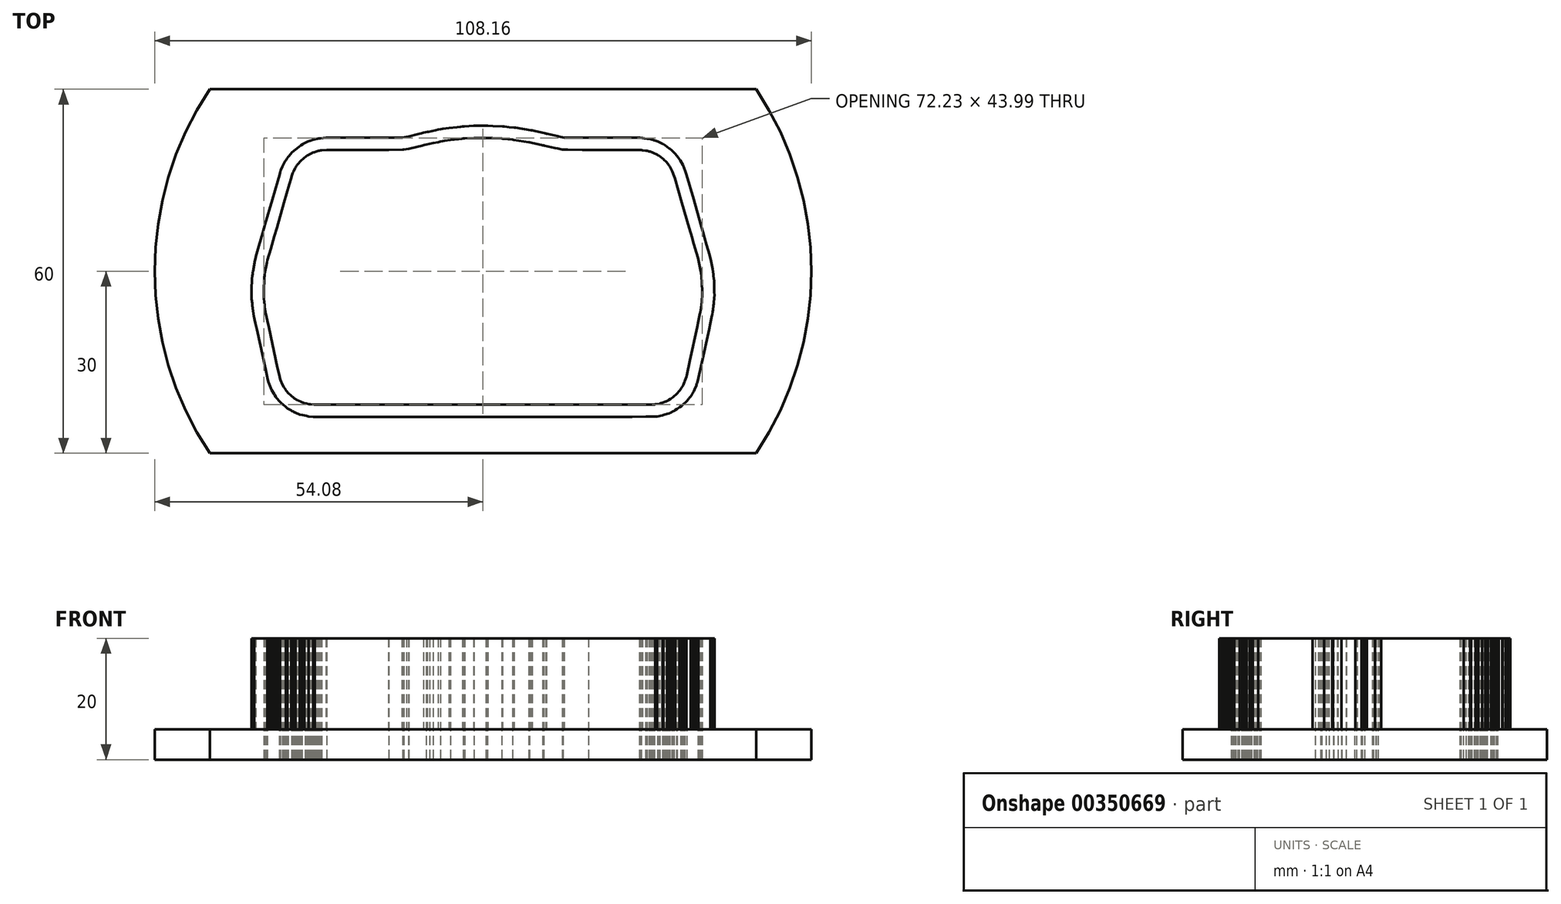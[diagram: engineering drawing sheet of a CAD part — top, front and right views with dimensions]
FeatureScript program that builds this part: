
annotation { "Feature Type Name" : "Feature", "Feature Type Description" : "" }
export const myFeature = defineFeature(function(context is Context, id is Id, definition is map)
    precondition{}
    {
        {
            var Q0;
            Q0=qCreatedBy(makeId("Top.planeOp"),FACE);
            var sketch = newSketch(context, id + "F0", { "sketchPlane" : qUnion([Q0])});
            skLineSegment(sketch, "E0.bottom", {"start": v(-45, 30) * mm, "end": v(45, 30) * mm});
            skLineSegment(sketch, "E0.top", {"start": v(-45, -30) * mm, "end": v(45, -30) * mm});
            skArc(sketch, "E1", {"start": v(-45, 30) * mm, "mid": v(-54.08, 0) * mm, "end": v(-45, -30) * mm});
            skArc(sketch, "E2.MirrorCS", {"start": v(45, 30) * mm, "mid": v(54.08, 0) * mm, "end": v(45, -30) * mm});
            skSolve(sketch);
        }
        {
            var Q0;
            Q0 = qSketchRegion(id + "F0", true);
            extrude(context, id + "F1", {"entities" : qUnion([Q0]), "depth" : 5 * mm});
        }
        {
            var Q0;
            Q0=makeQuery(id+"F1.opExtrude","CAP_FACE",FACE,{"disambiguationData":[OSD([sQuery(id+"F0.wireOp",EDGE,"E0.bottom"),sQuery(id+"F0.wireOp",EDGE,"E0.top"),sQuery(id+"F0.wireOp",EDGE,"E1"),sQuery(id+"F0.wireOp",EDGE,"E2.MirrorCS")])],"isStart":false});
            var sketch = newSketch(context, id + "F2", { "sketchPlane" : qUnion([Q0])});
            skLineSegment(sketch, "E3", {"start": v(-13.19, 20.04) * mm, "end": v(-13.22, 20.04) * mm});
            skLineSegment(sketch, "E4", {"start": v(-13.22, 20.04) * mm, "end": v(-15.53, 20) * mm});
            skLineSegment(sketch, "E5", {"start": v(-15.53, 20) * mm, "end": v(-16.38, 20) * mm});
            skLineSegment(sketch, "E6", {"start": v(-16.38, 20) * mm, "end": v(-22.09, 20.01) * mm});
            skLineSegment(sketch, "E7", {"start": v(-22.09, 20.01) * mm, "end": v(-24.58, 20) * mm});
            skLineSegment(sketch, "E8", {"start": v(-24.58, 20) * mm, "end": v(-25.75, 20) * mm});
            skLineSegment(sketch, "E9", {"start": v(-25.75, 20) * mm, "end": v(-26.54, 19.93) * mm});
            skLineSegment(sketch, "E10", {"start": v(-26.54, 19.93) * mm, "end": v(-26.56, 19.92) * mm});
            skLineSegment(sketch, "E11", {"start": v(-26.56, 19.92) * mm, "end": v(-26.73, 19.91) * mm});
            skLineSegment(sketch, "E12", {"start": v(-26.73, 19.91) * mm, "end": v(-26.77, 19.9) * mm});
            skLineSegment(sketch, "E13", {"start": v(-26.77, 19.9) * mm, "end": v(-26.93, 19.87) * mm});
            skLineSegment(sketch, "E14", {"start": v(-26.93, 19.87) * mm, "end": v(-27.02, 19.84) * mm});
            skLineSegment(sketch, "E15", {"start": v(-27.02, 19.84) * mm, "end": v(-27.07, 19.84) * mm});
            skLineSegment(sketch, "E16", {"start": v(-27.07, 19.84) * mm, "end": v(-27.29, 19.8) * mm});
            skLineSegment(sketch, "E17", {"start": v(-27.29, 19.8) * mm, "end": v(-27.43, 19.75) * mm});
            skLineSegment(sketch, "E18", {"start": v(-27.43, 19.75) * mm, "end": v(-27.8, 19.62) * mm});
            skLineSegment(sketch, "E19", {"start": v(-27.8, 19.62) * mm, "end": v(-27.85, 19.6) * mm});
            skLineSegment(sketch, "E20", {"start": v(-27.85, 19.6) * mm, "end": v(-28.06, 19.54) * mm});
            skLineSegment(sketch, "E21", {"start": v(-28.06, 19.54) * mm, "end": v(-28.09, 19.52) * mm});
            skLineSegment(sketch, "E22", {"start": v(-28.09, 19.52) * mm, "end": v(-28.16, 19.49) * mm});
            skLineSegment(sketch, "E23", {"start": v(-28.16, 19.49) * mm, "end": v(-28.67, 19.22) * mm});
            skLineSegment(sketch, "E24", {"start": v(-28.67, 19.22) * mm, "end": v(-28.75, 19.18) * mm});
            skLineSegment(sketch, "E25", {"start": v(-28.75, 19.18) * mm, "end": v(-28.93, 19.09) * mm});
            skLineSegment(sketch, "E26", {"start": v(-28.93, 19.09) * mm, "end": v(-29.1, 18.96) * mm});
            skLineSegment(sketch, "E27", {"start": v(-29.1, 18.96) * mm, "end": v(-30, 18.23) * mm});
            skLineSegment(sketch, "E28", {"start": v(-30, 18.23) * mm, "end": v(-30.47, 17.64) * mm});
            skLineSegment(sketch, "E29", {"start": v(-30.47, 17.64) * mm, "end": v(-30.6, 17.5) * mm});
            skLineSegment(sketch, "E30", {"start": v(-30.6, 17.5) * mm, "end": v(-30.67, 17.42) * mm});
            skLineSegment(sketch, "E31", {"start": v(-30.67, 17.42) * mm, "end": v(-30.74, 17.3) * mm});
            skLineSegment(sketch, "E32", {"start": v(-30.74, 17.3) * mm, "end": v(-30.9, 17.07) * mm});
            skLineSegment(sketch, "E33", {"start": v(-30.9, 17.07) * mm, "end": v(-30.92, 17.02) * mm});
            skLineSegment(sketch, "E34", {"start": v(-30.92, 17.02) * mm, "end": v(-30.93, 17.01) * mm});
            skLineSegment(sketch, "E35", {"start": v(-30.93, 17.01) * mm, "end": v(-31.22, 16.41) * mm});
            skLineSegment(sketch, "E36", {"start": v(-31.22, 16.41) * mm, "end": v(-31.31, 16.22) * mm});
            skLineSegment(sketch, "E37", {"start": v(-31.31, 16.22) * mm, "end": v(-31.31, 16.22) * mm});
            skLineSegment(sketch, "E38", {"start": v(-31.31, 16.22) * mm, "end": v(-31.44, 15.86) * mm});
            skLineSegment(sketch, "E39", {"start": v(-31.44, 15.86) * mm, "end": v(-31.5, 15.65) * mm});
            skLineSegment(sketch, "E40", {"start": v(-31.5, 15.65) * mm, "end": v(-31.58, 15.39) * mm});
            skLineSegment(sketch, "E41", {"start": v(-31.58, 15.39) * mm, "end": v(-31.89, 14.33) * mm});
            skLineSegment(sketch, "E42", {"start": v(-31.89, 14.33) * mm, "end": v(-32.77, 11.28) * mm});
            skLineSegment(sketch, "E43", {"start": v(-32.77, 11.28) * mm, "end": v(-33.95, 7.2) * mm});
            skLineSegment(sketch, "E44", {"start": v(-33.95, 7.2) * mm, "end": v(-34.35, 5.79) * mm});
            skLineSegment(sketch, "E45", {"start": v(-34.35, 5.79) * mm, "end": v(-34.96, 3.66) * mm});
            skLineSegment(sketch, "E46", {"start": v(-34.96, 3.66) * mm, "end": v(-35.48, 1.86) * mm});
            skLineSegment(sketch, "E47", {"start": v(-35.48, 1.86) * mm, "end": v(-35.5, 1.82) * mm});
            skLineSegment(sketch, "E48", {"start": v(-35.5, 1.82) * mm, "end": v(-35.58, 1.44) * mm});
            skLineSegment(sketch, "E49", {"start": v(-35.58, 1.44) * mm, "end": v(-35.94, -0.4) * mm});
            skLineSegment(sketch, "E50", {"start": v(-35.94, -0.4) * mm, "end": v(-35.94, -0.42) * mm});
            skLineSegment(sketch, "E51", {"start": v(-35.94, -0.42) * mm, "end": v(-35.97, -0.7) * mm});
            skLineSegment(sketch, "E52", {"start": v(-35.97, -0.7) * mm, "end": v(-36, -1) * mm});
            skLineSegment(sketch, "E53", {"start": v(-36, -1) * mm, "end": v(-36.05, -1.36) * mm});
            skLineSegment(sketch, "E54", {"start": v(-36.05, -1.36) * mm, "end": v(-36.1, -3.07) * mm});
            skLineSegment(sketch, "E55", {"start": v(-36.1, -3.07) * mm, "end": v(-36.11, -3.77) * mm});
            skLineSegment(sketch, "E56", {"start": v(-36.11, -3.77) * mm, "end": v(-36.09, -4.44) * mm});
            skLineSegment(sketch, "E57", {"start": v(-36.09, -4.44) * mm, "end": v(-36.02, -5.1) * mm});
            skLineSegment(sketch, "E58", {"start": v(-36.02, -5.1) * mm, "end": v(-35.98, -5.52) * mm});
            skLineSegment(sketch, "E59", {"start": v(-35.98, -5.52) * mm, "end": v(-35.95, -5.78) * mm});
            skLineSegment(sketch, "E60", {"start": v(-35.95, -5.78) * mm, "end": v(-35.94, -5.86) * mm});
            skLineSegment(sketch, "E61", {"start": v(-35.94, -5.86) * mm, "end": v(-35.75, -7.07) * mm});
            skLineSegment(sketch, "E62", {"start": v(-35.75, -7.07) * mm, "end": v(-35.7, -7.25) * mm});
            skLineSegment(sketch, "E63", {"start": v(-35.7, -7.25) * mm, "end": v(-35.64, -7.56) * mm});
            skLineSegment(sketch, "E64", {"start": v(-35.64, -7.56) * mm, "end": v(-35.52, -8.14) * mm});
            skLineSegment(sketch, "E65", {"start": v(-35.52, -8.14) * mm, "end": v(-35.29, -9.19) * mm});
            skLineSegment(sketch, "E66", {"start": v(-35.29, -9.19) * mm, "end": v(-33.84, -15.86) * mm});
            skLineSegment(sketch, "E67", {"start": v(-33.84, -15.86) * mm, "end": v(-33.57, -17.1) * mm});
            skLineSegment(sketch, "E68", {"start": v(-33.57, -17.1) * mm, "end": v(-33.5, -17.38) * mm});
            skLineSegment(sketch, "E69", {"start": v(-33.5, -17.38) * mm, "end": v(-33.42, -17.7) * mm});
            skLineSegment(sketch, "E70", {"start": v(-33.42, -17.7) * mm, "end": v(-33.34, -17.9) * mm});
            skLineSegment(sketch, "E71", {"start": v(-33.34, -17.9) * mm, "end": v(-33.05, -18.64) * mm});
            skLineSegment(sketch, "E72", {"start": v(-33.05, -18.64) * mm, "end": v(-32.77, -19.1) * mm});
            skLineSegment(sketch, "E73", {"start": v(-32.77, -19.1) * mm, "end": v(-32.76, -19.1) * mm});
            skLineSegment(sketch, "E74", {"start": v(-32.76, -19.1) * mm, "end": v(-32.57, -19.4) * mm});
            skLineSegment(sketch, "E75", {"start": v(-32.57, -19.4) * mm, "end": v(-32.5, -19.55) * mm});
            skLineSegment(sketch, "E76", {"start": v(-32.5, -19.55) * mm, "end": v(-32.44, -19.6) * mm});
            skLineSegment(sketch, "E77", {"start": v(-32.44, -19.6) * mm, "end": v(-32.24, -19.84) * mm});
            skLineSegment(sketch, "E78", {"start": v(-32.24, -19.84) * mm, "end": v(-32.12, -20.01) * mm});
            skLineSegment(sketch, "E79", {"start": v(-32.12, -20.01) * mm, "end": v(-32.06, -20.08) * mm});
            skLineSegment(sketch, "E80", {"start": v(-32.06, -20.08) * mm, "end": v(-32, -20.13) * mm});
            skLineSegment(sketch, "E81", {"start": v(-32, -20.13) * mm, "end": v(-31.69, -20.4) * mm});
            skLineSegment(sketch, "E82", {"start": v(-31.69, -20.4) * mm, "end": v(-31.58, -20.5) * mm});
            skLineSegment(sketch, "E83", {"start": v(-31.58, -20.5) * mm, "end": v(-31.2, -20.83) * mm});
            skLineSegment(sketch, "E84", {"start": v(-31.2, -20.83) * mm, "end": v(-31.12, -20.9) * mm});
            skLineSegment(sketch, "E85", {"start": v(-31.12, -20.9) * mm, "end": v(-31.12, -20.9) * mm});
            skLineSegment(sketch, "E86", {"start": v(-31.12, -20.9) * mm, "end": v(-31.05, -20.95) * mm});
            skLineSegment(sketch, "E87", {"start": v(-31.05, -20.95) * mm, "end": v(-30.61, -21.22) * mm});
            skLineSegment(sketch, "E88", {"start": v(-30.61, -21.22) * mm, "end": v(-30.57, -21.24) * mm});
            skLineSegment(sketch, "E89", {"start": v(-30.57, -21.24) * mm, "end": v(-30.38, -21.32) * mm});
            skLineSegment(sketch, "E90", {"start": v(-30.38, -21.32) * mm, "end": v(-30.33, -21.35) * mm});
            skLineSegment(sketch, "E91", {"start": v(-30.33, -21.35) * mm, "end": v(-30.13, -21.44) * mm});
            skLineSegment(sketch, "E92", {"start": v(-30.13, -21.44) * mm, "end": v(-30.07, -21.48) * mm});
            skLineSegment(sketch, "E93", {"start": v(-30.07, -21.48) * mm, "end": v(-30.05, -21.49) * mm});
            skLineSegment(sketch, "E94", {"start": v(-30.05, -21.49) * mm, "end": v(-29.8, -21.6) * mm});
            skLineSegment(sketch, "E95", {"start": v(-29.8, -21.6) * mm, "end": v(-29.78, -21.6) * mm});
            skLineSegment(sketch, "E96", {"start": v(-29.78, -21.6) * mm, "end": v(-29.27, -21.77) * mm});
            skLineSegment(sketch, "E97", {"start": v(-29.27, -21.77) * mm, "end": v(-29.07, -21.8) * mm});
            skLineSegment(sketch, "E98", {"start": v(-29.07, -21.8) * mm, "end": v(-28.67, -21.89) * mm});
            skLineSegment(sketch, "E99", {"start": v(-28.67, -21.89) * mm, "end": v(-28.43, -21.94) * mm});
            skLineSegment(sketch, "E100", {"start": v(-28.43, -21.94) * mm, "end": v(-27.8, -21.99) * mm});
            skLineSegment(sketch, "E101", {"start": v(-27.8, -21.99) * mm, "end": v(-27.64, -22) * mm});
            skLineSegment(sketch, "E102", {"start": v(-27.64, -22) * mm, "end": v(0.52, -22) * mm});
            skLineSegment(sketch, "E103", {"start": v(0.52, -22) * mm, "end": v(2.71, -22) * mm});
            skLineSegment(sketch, "E104", {"start": v(2.71, -22) * mm, "end": v(8.2, -22) * mm});
            skLineSegment(sketch, "E105", {"start": v(8.2, -22) * mm, "end": v(16.38, -22) * mm});
            skLineSegment(sketch, "E106", {"start": v(16.38, -22) * mm, "end": v(23.57, -22) * mm});
            skLineSegment(sketch, "E107", {"start": v(23.57, -22) * mm, "end": v(24.58, -21.99) * mm});
            skLineSegment(sketch, "E108", {"start": v(24.58, -21.99) * mm, "end": v(26.86, -21.97) * mm});
            skLineSegment(sketch, "E109", {"start": v(26.86, -21.97) * mm, "end": v(28.22, -21.96) * mm});
            skLineSegment(sketch, "E110", {"start": v(28.22, -21.96) * mm, "end": v(28.25, -21.96) * mm});
            skLineSegment(sketch, "E111", {"start": v(28.25, -21.96) * mm, "end": v(28.37, -21.94) * mm});
            skLineSegment(sketch, "E112", {"start": v(28.37, -21.94) * mm, "end": v(29.06, -21.82) * mm});
            skLineSegment(sketch, "E113", {"start": v(29.06, -21.82) * mm, "end": v(29.09, -21.81) * mm});
            skLineSegment(sketch, "E114", {"start": v(29.09, -21.81) * mm, "end": v(29.11, -21.8) * mm});
            skLineSegment(sketch, "E115", {"start": v(29.11, -21.8) * mm, "end": v(29.78, -21.6) * mm});
            skLineSegment(sketch, "E116", {"start": v(29.78, -21.6) * mm, "end": v(29.9, -21.56) * mm});
            skLineSegment(sketch, "E117", {"start": v(29.9, -21.56) * mm, "end": v(29.91, -21.55) * mm});
            skLineSegment(sketch, "E118", {"start": v(29.91, -21.55) * mm, "end": v(30.08, -21.48) * mm});
            skLineSegment(sketch, "E119", {"start": v(30.08, -21.48) * mm, "end": v(30.14, -21.45) * mm});
            skLineSegment(sketch, "E120", {"start": v(30.14, -21.45) * mm, "end": v(30.37, -21.34) * mm});
            skLineSegment(sketch, "E121", {"start": v(30.37, -21.34) * mm, "end": v(30.54, -21.26) * mm});
            skLineSegment(sketch, "E122", {"start": v(30.54, -21.26) * mm, "end": v(30.56, -21.24) * mm});
            skLineSegment(sketch, "E123", {"start": v(30.56, -21.24) * mm, "end": v(30.88, -21.03) * mm});
            skLineSegment(sketch, "E124", {"start": v(30.88, -21.03) * mm, "end": v(31.26, -20.77) * mm});
            skLineSegment(sketch, "E125", {"start": v(31.26, -20.77) * mm, "end": v(31.43, -20.66) * mm});
            skLineSegment(sketch, "E126", {"start": v(31.43, -20.66) * mm, "end": v(31.84, -20.29) * mm});
            skLineSegment(sketch, "E127", {"start": v(31.84, -20.29) * mm, "end": v(31.92, -20.22) * mm});
            skLineSegment(sketch, "E128", {"start": v(31.92, -20.22) * mm, "end": v(31.95, -20.19) * mm});
            skLineSegment(sketch, "E129", {"start": v(31.95, -20.19) * mm, "end": v(31.98, -20.16) * mm});
            skLineSegment(sketch, "E130", {"start": v(31.98, -20.16) * mm, "end": v(32.33, -19.73) * mm});
            skLineSegment(sketch, "E131", {"start": v(32.33, -19.73) * mm, "end": v(32.43, -19.61) * mm});
            skLineSegment(sketch, "E132", {"start": v(32.43, -19.61) * mm, "end": v(32.58, -19.43) * mm});
            skLineSegment(sketch, "E133", {"start": v(32.58, -19.43) * mm, "end": v(32.68, -19.27) * mm});
            skLineSegment(sketch, "E134", {"start": v(32.68, -19.27) * mm, "end": v(32.7, -19.24) * mm});
            skLineSegment(sketch, "E135", {"start": v(32.7, -19.24) * mm, "end": v(32.77, -19.13) * mm});
            skLineSegment(sketch, "E136", {"start": v(32.77, -19.13) * mm, "end": v(32.93, -18.86) * mm});
            skLineSegment(sketch, "E137", {"start": v(32.93, -18.86) * mm, "end": v(32.97, -18.77) * mm});
            skLineSegment(sketch, "E138", {"start": v(32.97, -18.77) * mm, "end": v(32.98, -18.75) * mm});
            skLineSegment(sketch, "E139", {"start": v(32.98, -18.75) * mm, "end": v(33.06, -18.58) * mm});
            skLineSegment(sketch, "E140", {"start": v(33.06, -18.58) * mm, "end": v(33.22, -18.24) * mm});
            skLineSegment(sketch, "E141", {"start": v(33.22, -18.24) * mm, "end": v(33.24, -18.2) * mm});
            skLineSegment(sketch, "E142", {"start": v(33.24, -18.2) * mm, "end": v(33.28, -18.06) * mm});
            skLineSegment(sketch, "E143", {"start": v(33.28, -18.06) * mm, "end": v(33.5, -17.4) * mm});
            skLineSegment(sketch, "E144", {"start": v(33.5, -17.4) * mm, "end": v(33.5, -17.38) * mm});
            skLineSegment(sketch, "E145", {"start": v(33.5, -17.38) * mm, "end": v(33.5, -17.38) * mm});
            skLineSegment(sketch, "E146", {"start": v(33.5, -17.38) * mm, "end": v(33.56, -17.13) * mm});
            skLineSegment(sketch, "E147", {"start": v(33.56, -17.13) * mm, "end": v(34.09, -14.66) * mm});
            skLineSegment(sketch, "E148", {"start": v(34.09, -14.66) * mm, "end": v(35.28, -9.19) * mm});
            skLineSegment(sketch, "E149", {"start": v(35.28, -9.19) * mm, "end": v(35.5, -8.17) * mm});
            skLineSegment(sketch, "E150", {"start": v(35.5, -8.17) * mm, "end": v(35.76, -6.92) * mm});
            skLineSegment(sketch, "E151", {"start": v(35.76, -6.92) * mm, "end": v(35.78, -6.78) * mm});
            skLineSegment(sketch, "E152", {"start": v(35.78, -6.78) * mm, "end": v(35.87, -6.38) * mm});
            skLineSegment(sketch, "E153", {"start": v(35.87, -6.38) * mm, "end": v(35.9, -6.07) * mm});
            skLineSegment(sketch, "E154", {"start": v(35.9, -6.07) * mm, "end": v(36, -5.42) * mm});
            skLineSegment(sketch, "E155", {"start": v(36, -5.42) * mm, "end": v(36.03, -5.15) * mm});
            skLineSegment(sketch, "E156", {"start": v(36.03, -5.15) * mm, "end": v(36.03, -5.1) * mm});
            skLineSegment(sketch, "E157", {"start": v(36.03, -5.1) * mm, "end": v(36.04, -4.94) * mm});
            skLineSegment(sketch, "E158", {"start": v(36.04, -4.94) * mm, "end": v(36.11, -3.83) * mm});
            skLineSegment(sketch, "E159", {"start": v(36.11, -3.83) * mm, "end": v(36.1, -3.51) * mm});
            skLineSegment(sketch, "E160", {"start": v(36.1, -3.51) * mm, "end": v(36.07, -1.8) * mm});
            skLineSegment(sketch, "E161", {"start": v(36.07, -1.8) * mm, "end": v(36.07, -1.7) * mm});
            skLineSegment(sketch, "E162", {"start": v(36.07, -1.7) * mm, "end": v(36, -1) * mm});
            skLineSegment(sketch, "E163", {"start": v(36, -1) * mm, "end": v(35.97, -0.72) * mm});
            skLineSegment(sketch, "E164", {"start": v(35.97, -0.72) * mm, "end": v(35.96, -0.63) * mm});
            skLineSegment(sketch, "E165", {"start": v(35.96, -0.63) * mm, "end": v(35.96, -0.62) * mm});
            skLineSegment(sketch, "E166", {"start": v(35.96, -0.62) * mm, "end": v(35.93, -0.4) * mm});
            skLineSegment(sketch, "E167", {"start": v(35.93, -0.4) * mm, "end": v(35.85, -0.02) * mm});
            skLineSegment(sketch, "E168", {"start": v(35.85, -0.02) * mm, "end": v(35.63, 1.25) * mm});
            skLineSegment(sketch, "E169", {"start": v(35.63, 1.25) * mm, "end": v(35.4, 2.2) * mm});
            skLineSegment(sketch, "E170", {"start": v(35.4, 2.2) * mm, "end": v(34.92, 3.85) * mm});
            skLineSegment(sketch, "E171", {"start": v(34.92, 3.85) * mm, "end": v(34.6, 4.94) * mm});
            skLineSegment(sketch, "E172", {"start": v(34.6, 4.94) * mm, "end": v(34.44, 5.5) * mm});
            skLineSegment(sketch, "E173", {"start": v(34.44, 5.5) * mm, "end": v(33.95, 7.2) * mm});
            skLineSegment(sketch, "E174", {"start": v(33.95, 7.2) * mm, "end": v(32.77, 11.29) * mm});
            skLineSegment(sketch, "E175", {"start": v(32.77, 11.29) * mm, "end": v(31.58, 15.39) * mm});
            skLineSegment(sketch, "E176", {"start": v(31.58, 15.39) * mm, "end": v(31.5, 15.65) * mm});
            skLineSegment(sketch, "E177", {"start": v(31.5, 15.65) * mm, "end": v(31.17, 16.51) * mm});
            skLineSegment(sketch, "E178", {"start": v(31.17, 16.51) * mm, "end": v(31.12, 16.64) * mm});
            skLineSegment(sketch, "E179", {"start": v(31.12, 16.64) * mm, "end": v(31.12, 16.65) * mm});
            skLineSegment(sketch, "E180", {"start": v(31.12, 16.65) * mm, "end": v(30.78, 17.24) * mm});
            skLineSegment(sketch, "E181", {"start": v(30.78, 17.24) * mm, "end": v(30.71, 17.35) * mm});
            skLineSegment(sketch, "E182", {"start": v(30.71, 17.35) * mm, "end": v(30.64, 17.43) * mm});
            skLineSegment(sketch, "E183", {"start": v(30.64, 17.43) * mm, "end": v(30.18, 18.03) * mm});
            skLineSegment(sketch, "E184", {"start": v(30.18, 18.03) * mm, "end": v(29.78, 18.44) * mm});
            skLineSegment(sketch, "E185", {"start": v(29.78, 18.44) * mm, "end": v(29.77, 18.44) * mm});
            skLineSegment(sketch, "E186", {"start": v(29.77, 18.44) * mm, "end": v(29.57, 18.6) * mm});
            skLineSegment(sketch, "E187", {"start": v(29.57, 18.6) * mm, "end": v(29.56, 18.6) * mm});
            skLineSegment(sketch, "E188", {"start": v(29.56, 18.6) * mm, "end": v(28.95, 19.08) * mm});
            skLineSegment(sketch, "E189", {"start": v(28.95, 19.08) * mm, "end": v(28.9, 19.1) * mm});
            skLineSegment(sketch, "E190", {"start": v(28.9, 19.1) * mm, "end": v(28.77, 19.17) * mm});
            skLineSegment(sketch, "E191", {"start": v(28.77, 19.17) * mm, "end": v(28.73, 19.19) * mm});
            skLineSegment(sketch, "E192", {"start": v(28.73, 19.19) * mm, "end": v(28.67, 19.22) * mm});
            skLineSegment(sketch, "E193", {"start": v(28.67, 19.22) * mm, "end": v(28.14, 19.49) * mm});
            skLineSegment(sketch, "E194", {"start": v(28.14, 19.49) * mm, "end": v(28, 19.56) * mm});
            skLineSegment(sketch, "E195", {"start": v(28, 19.56) * mm, "end": v(27.86, 19.61) * mm});
            skLineSegment(sketch, "E196", {"start": v(27.86, 19.61) * mm, "end": v(27.76, 19.63) * mm});
            skLineSegment(sketch, "E197", {"start": v(27.76, 19.63) * mm, "end": v(27.7, 19.65) * mm});
            skLineSegment(sketch, "E198", {"start": v(27.7, 19.65) * mm, "end": v(27.52, 19.71) * mm});
            skLineSegment(sketch, "E199", {"start": v(27.52, 19.71) * mm, "end": v(27.35, 19.77) * mm});
            skLineSegment(sketch, "E200", {"start": v(27.35, 19.77) * mm, "end": v(27.23, 19.8) * mm});
            skLineSegment(sketch, "E201", {"start": v(27.23, 19.8) * mm, "end": v(27.06, 19.85) * mm});
            skLineSegment(sketch, "E202", {"start": v(27.06, 19.85) * mm, "end": v(26.78, 19.88) * mm});
            skLineSegment(sketch, "E203", {"start": v(26.78, 19.88) * mm, "end": v(26.3, 19.96) * mm});
            skLineSegment(sketch, "E204", {"start": v(26.3, 19.96) * mm, "end": v(26.06, 20) * mm});
            skLineSegment(sketch, "E205", {"start": v(26.06, 20) * mm, "end": v(25.8, 20) * mm});
            skLineSegment(sketch, "E206", {"start": v(25.8, 20) * mm, "end": v(25.74, 20) * mm});
            skLineSegment(sketch, "E207", {"start": v(25.74, 20) * mm, "end": v(17.38, 20) * mm});
            skLineSegment(sketch, "E208", {"start": v(17.38, 20) * mm, "end": v(16.38, 20.02) * mm});
            skLineSegment(sketch, "E209", {"start": v(16.38, 20.02) * mm, "end": v(13.97, 20.04) * mm});
            skLineSegment(sketch, "E210", {"start": v(13.97, 20.04) * mm, "end": v(13.22, 20.04) * mm});
            skLineSegment(sketch, "E211", {"start": v(13.22, 20.04) * mm, "end": v(13.15, 20.04) * mm});
            skLineSegment(sketch, "E212", {"start": v(13.15, 20.04) * mm, "end": v(13.11, 20.05) * mm});
            skLineSegment(sketch, "E213", {"start": v(13.11, 20.05) * mm, "end": v(13.06, 20.06) * mm});
            skLineSegment(sketch, "E214", {"start": v(13.06, 20.06) * mm, "end": v(12.29, 20.23) * mm});
            skLineSegment(sketch, "E215", {"start": v(12.29, 20.23) * mm, "end": v(11.88, 20.31) * mm});
            skLineSegment(sketch, "E216", {"start": v(11.88, 20.31) * mm, "end": v(10.12, 20.7) * mm});
            skLineSegment(sketch, "E217", {"start": v(10.12, 20.7) * mm, "end": v(9.99, 20.73) * mm});
            skLineSegment(sketch, "E218", {"start": v(9.99, 20.73) * mm, "end": v(9.85, 20.77) * mm});
            skLineSegment(sketch, "E219", {"start": v(9.85, 20.77) * mm, "end": v(9.84, 20.77) * mm});
            skLineSegment(sketch, "E220", {"start": v(9.84, 20.77) * mm, "end": v(9.64, 20.82) * mm});
            skLineSegment(sketch, "E221", {"start": v(9.64, 20.82) * mm, "end": v(8.2, 21.14) * mm});
            skLineSegment(sketch, "E222", {"start": v(8.2, 21.14) * mm, "end": v(7.67, 21.26) * mm});
            skLineSegment(sketch, "E223", {"start": v(7.67, 21.26) * mm, "end": v(7.54, 21.28) * mm});
            skLineSegment(sketch, "E224", {"start": v(7.54, 21.28) * mm, "end": v(5.06, 21.68) * mm});
            skLineSegment(sketch, "E225", {"start": v(5.06, 21.68) * mm, "end": v(4.85, 21.7) * mm});
            skLineSegment(sketch, "E226", {"start": v(4.85, 21.7) * mm, "end": v(4.1, 21.78) * mm});
            skLineSegment(sketch, "E227", {"start": v(4.1, 21.78) * mm, "end": v(3.3, 21.86) * mm});
            skLineSegment(sketch, "E228", {"start": v(3.3, 21.86) * mm, "end": v(3.06, 21.89) * mm});
            skLineSegment(sketch, "E229", {"start": v(3.06, 21.89) * mm, "end": v(1.56, 21.95) * mm});
            skLineSegment(sketch, "E230", {"start": v(1.56, 21.95) * mm, "end": v(0.72, 21.99) * mm});
            skLineSegment(sketch, "E231", {"start": v(0.72, 21.99) * mm, "end": v(0.48, 22) * mm});
            skLineSegment(sketch, "E232", {"start": v(0.48, 22) * mm, "end": v(0, 22) * mm});
            skLineSegment(sketch, "E233", {"start": v(0, 22) * mm, "end": v(-1, 21.98) * mm});
            skLineSegment(sketch, "E234", {"start": v(-1, 21.98) * mm, "end": v(-1.44, 21.97) * mm});
            skLineSegment(sketch, "E235", {"start": v(-1.44, 21.97) * mm, "end": v(-2.98, 21.88) * mm});
            skLineSegment(sketch, "E236", {"start": v(-2.98, 21.88) * mm, "end": v(-3.24, 21.87) * mm});
            skLineSegment(sketch, "E237", {"start": v(-3.24, 21.87) * mm, "end": v(-3.48, 21.85) * mm});
            skLineSegment(sketch, "E238", {"start": v(-3.48, 21.85) * mm, "end": v(-4.03, 21.78) * mm});
            skLineSegment(sketch, "E239", {"start": v(-4.03, 21.78) * mm, "end": v(-5.37, 21.64) * mm});
            skLineSegment(sketch, "E240", {"start": v(-5.37, 21.64) * mm, "end": v(-6.32, 21.49) * mm});
            skLineSegment(sketch, "E241", {"start": v(-6.32, 21.49) * mm, "end": v(-6.6, 21.44) * mm});
            skLineSegment(sketch, "E242", {"start": v(-6.6, 21.44) * mm, "end": v(-7, 21.38) * mm});
            skLineSegment(sketch, "E243", {"start": v(-7, 21.38) * mm, "end": v(-7.39, 21.3) * mm});
            skLineSegment(sketch, "E244", {"start": v(-7.39, 21.3) * mm, "end": v(-8.2, 21.13) * mm});
            skLineSegment(sketch, "E245", {"start": v(-8.2, 21.13) * mm, "end": v(-8.2, 21.12) * mm});
            skLineSegment(sketch, "E246", {"start": v(-8.2, 21.12) * mm, "end": v(-8.8, 21) * mm});
            skLineSegment(sketch, "E247", {"start": v(-8.8, 21) * mm, "end": v(-9.35, 20.9) * mm});
            skLineSegment(sketch, "E248", {"start": v(-9.35, 20.9) * mm, "end": v(-9.7, 20.8) * mm});
            skLineSegment(sketch, "E249", {"start": v(-9.7, 20.8) * mm, "end": v(-10.03, 20.72) * mm});
            skLineSegment(sketch, "E250", {"start": v(-10.03, 20.72) * mm, "end": v(-11.95, 20.24) * mm});
            skLineSegment(sketch, "E251", {"start": v(-11.95, 20.24) * mm, "end": v(-12.22, 20.17) * mm});
            skLineSegment(sketch, "E252", {"start": v(-12.22, 20.17) * mm, "end": v(-12.24, 20.17) * mm});
            skLineSegment(sketch, "E253", {"start": v(-12.24, 20.17) * mm, "end": v(-12.29, 20.16) * mm});
            skLineSegment(sketch, "E254", {"start": v(-12.29, 20.16) * mm, "end": v(-13.02, 20.07) * mm});
            skLineSegment(sketch, "E255", {"start": v(-13.02, 20.07) * mm, "end": v(-13.14, 20.05) * mm});
            skLineSegment(sketch, "E256", {"start": v(-13.14, 20.05) * mm, "end": v(-13.19, 20.04) * mm});
            skSolve(sketch);
        }
        {
            var Q0;
            Q0=makeQuery(id+"F2.imprint","IMPRINT",FACE,{"disambiguationData":[TD([[makeQuery(id+"F2.imprint","IMPRINT",EDGE,{"derivedFrom":sQuery(id+"F2.wireOp",EDGE,"E3")}),-1.0]])]});
            var sketch = newSketch(context, id + "F3", { "sketchPlane" : qUnion([Q0])});
            skLineSegment(sketch, "E257.0", {"start": v(-13.31, 22.04) * mm, "end": v(-13.33, 22.04) * mm});
            skLineSegment(sketch, "E257.1", {"start": v(-12.6, 22.14) * mm, "end": v(-13.31, 22.04) * mm});
            skLineSegment(sketch, "E257.2", {"start": v(-12.44, 22.18) * mm, "end": v(-12.6, 22.14) * mm});
            skLineSegment(sketch, "E257.3", {"start": v(-10.52, 22.66) * mm, "end": v(-12.44, 22.18) * mm});
            skLineSegment(sketch, "E257.4", {"start": v(-10.18, 22.75) * mm, "end": v(-10.52, 22.66) * mm});
            skLineSegment(sketch, "E257.5", {"start": v(-9.77, 22.85) * mm, "end": v(-10.18, 22.75) * mm});
            skLineSegment(sketch, "E257.6", {"start": v(-9.2, 22.96) * mm, "end": v(-9.77, 22.85) * mm});
            skLineSegment(sketch, "E257.7", {"start": v(-8.96, 23) * mm, "end": v(-9.2, 22.96) * mm});
            skLineSegment(sketch, "E257.8", {"start": v(-7.8, 23.25) * mm, "end": v(-8.96, 23) * mm});
            skLineSegment(sketch, "E257.9", {"start": v(-7.37, 23.35) * mm, "end": v(-7.8, 23.25) * mm});
            skLineSegment(sketch, "E257.10", {"start": v(-6.91, 23.42) * mm, "end": v(-7.37, 23.35) * mm});
            skLineSegment(sketch, "E257.11", {"start": v(-6.63, 23.46) * mm, "end": v(-6.91, 23.42) * mm});
            skLineSegment(sketch, "E257.12", {"start": v(-5.63, 23.62) * mm, "end": v(-6.63, 23.46) * mm});
            skLineSegment(sketch, "E257.13", {"start": v(-4.25, 23.77) * mm, "end": v(-5.63, 23.62) * mm});
            skLineSegment(sketch, "E257.14", {"start": v(-3.7, 23.83) * mm, "end": v(-4.25, 23.77) * mm});
            skLineSegment(sketch, "E257.15", {"start": v(-3.36, 23.87) * mm, "end": v(-3.7, 23.83) * mm});
            skLineSegment(sketch, "E257.16", {"start": v(-3.07, 23.87) * mm, "end": v(-3.36, 23.87) * mm});
            skLineSegment(sketch, "E257.17", {"start": v(-1.52, 23.97) * mm, "end": v(-3.07, 23.87) * mm});
            skLineSegment(sketch, "E257.18", {"start": v(-1.03, 23.98) * mm, "end": v(-1.52, 23.97) * mm});
            skLineSegment(sketch, "E257.19", {"start": v(-0.02, 24) * mm, "end": v(-1.03, 23.98) * mm});
            skLineSegment(sketch, "E257.20", {"start": v(0.5, 24) * mm, "end": v(-0.02, 24) * mm});
            skLineSegment(sketch, "E257.21", {"start": v(0.8, 23.99) * mm, "end": v(0.5, 24) * mm});
            skLineSegment(sketch, "E257.22", {"start": v(1.65, 23.95) * mm, "end": v(0.8, 23.99) * mm});
            skLineSegment(sketch, "E257.23", {"start": v(3.2, 23.88) * mm, "end": v(1.65, 23.95) * mm});
            skLineSegment(sketch, "E257.24", {"start": v(3.5, 23.85) * mm, "end": v(3.2, 23.88) * mm});
            skLineSegment(sketch, "E257.25", {"start": v(4.3, 23.77) * mm, "end": v(3.5, 23.85) * mm});
            skLineSegment(sketch, "E257.26", {"start": v(5.1, 23.7) * mm, "end": v(4.3, 23.77) * mm});
            skLineSegment(sketch, "E257.27", {"start": v(5.37, 23.65) * mm, "end": v(5.1, 23.7) * mm});
            skLineSegment(sketch, "E257.28", {"start": v(7.9, 23.25) * mm, "end": v(5.37, 23.65) * mm});
            skLineSegment(sketch, "E257.29", {"start": v(8.1, 23.21) * mm, "end": v(7.9, 23.25) * mm});
            skLineSegment(sketch, "E257.30", {"start": v(8.63, 23.1) * mm, "end": v(8.1, 23.21) * mm});
            skLineSegment(sketch, "E257.31", {"start": v(10.08, 22.77) * mm, "end": v(8.63, 23.1) * mm});
            skLineSegment(sketch, "E257.32", {"start": v(10.28, 22.72) * mm, "end": v(10.08, 22.77) * mm});
            skLineSegment(sketch, "E257.33", {"start": v(10.35, 22.7) * mm, "end": v(10.28, 22.72) * mm});
            skLineSegment(sketch, "E257.34", {"start": v(10.48, 22.67) * mm, "end": v(10.35, 22.7) * mm});
            skLineSegment(sketch, "E257.35", {"start": v(10.55, 22.65) * mm, "end": v(10.48, 22.67) * mm});
            skLineSegment(sketch, "E257.36", {"start": v(12.3, 22.27) * mm, "end": v(10.55, 22.65) * mm});
            skLineSegment(sketch, "E257.37", {"start": v(12.71, 22.18) * mm, "end": v(12.3, 22.27) * mm});
            skLineSegment(sketch, "E257.38", {"start": v(13.36, 22.04) * mm, "end": v(12.71, 22.18) * mm});
            skLineSegment(sketch, "E257.39", {"start": v(-27.69, -24) * mm, "end": v(0.52, -24) * mm});
            skLineSegment(sketch, "E257.40", {"start": v(-27.93, -23.98) * mm, "end": v(-27.69, -24) * mm});
            skLineSegment(sketch, "E257.41", {"start": v(-28.7, -23.92) * mm, "end": v(-27.93, -23.98) * mm});
            skLineSegment(sketch, "E257.42", {"start": v(-29.08, -23.85) * mm, "end": v(-28.7, -23.92) * mm});
            skLineSegment(sketch, "E257.43", {"start": v(-29.44, -23.77) * mm, "end": v(-29.08, -23.85) * mm});
            skLineSegment(sketch, "E257.44", {"start": v(-29.76, -23.72) * mm, "end": v(-29.44, -23.77) * mm});
            skLineSegment(sketch, "E257.45", {"start": v(-30.11, -23.6) * mm, "end": v(-29.76, -23.72) * mm});
            skLineSegment(sketch, "E257.46", {"start": v(-30.2, -23.6) * mm, "end": v(-30.11, -23.6) * mm});
            skLineSegment(sketch, "E257.47", {"start": v(-30.9, -23.3) * mm, "end": v(-30.2, -23.6) * mm});
            skLineSegment(sketch, "E257.48", {"start": v(-31.02, -23.24) * mm, "end": v(-30.9, -23.3) * mm});
            skLineSegment(sketch, "E257.49", {"start": v(-31.06, -23.22) * mm, "end": v(-31.02, -23.24) * mm});
            skLineSegment(sketch, "E257.50", {"start": v(-31.18, -23.16) * mm, "end": v(-31.06, -23.22) * mm});
            skLineSegment(sketch, "E257.51", {"start": v(-31.22, -23.14) * mm, "end": v(-31.18, -23.16) * mm});
            skLineSegment(sketch, "E257.52", {"start": v(-31.45, -23.03) * mm, "end": v(-31.22, -23.14) * mm});
            skLineSegment(sketch, "E257.53", {"start": v(-31.6, -22.96) * mm, "end": v(-31.45, -23.03) * mm});
            skLineSegment(sketch, "E257.54", {"start": v(-32.2, -22.59) * mm, "end": v(-31.6, -22.96) * mm});
            skLineSegment(sketch, "E257.55", {"start": v(-32.36, -22.46) * mm, "end": v(-32.2, -22.59) * mm});
            skLineSegment(sketch, "E257.56", {"start": v(-32.47, -22.38) * mm, "end": v(-32.36, -22.46) * mm});
            skLineSegment(sketch, "E257.57", {"start": v(-32.9, -22) * mm, "end": v(-32.47, -22.38) * mm});
            skLineSegment(sketch, "E257.58", {"start": v(-33, -21.9) * mm, "end": v(-32.9, -22) * mm});
            skLineSegment(sketch, "E257.59", {"start": v(-33.32, -21.63) * mm, "end": v(-33, -21.9) * mm});
            skLineSegment(sketch, "E257.60", {"start": v(-33.45, -21.52) * mm, "end": v(-33.32, -21.63) * mm});
            skLineSegment(sketch, "E257.61", {"start": v(-33.66, -21.3) * mm, "end": v(-33.45, -21.52) * mm});
            skLineSegment(sketch, "E257.62", {"start": v(-33.82, -21.07) * mm, "end": v(-33.66, -21.3) * mm});
            skLineSegment(sketch, "E257.63", {"start": v(-33.96, -20.9) * mm, "end": v(-33.82, -21.07) * mm});
            skLineSegment(sketch, "E257.64", {"start": v(-34.14, -20.7) * mm, "end": v(-33.96, -20.9) * mm});
            skLineSegment(sketch, "E257.65", {"start": v(-34.3, -20.4) * mm, "end": v(-34.14, -20.7) * mm});
            skLineSegment(sketch, "E257.66", {"start": v(-34.38, -20.28) * mm, "end": v(-34.3, -20.4) * mm});
            skLineSegment(sketch, "E257.67", {"start": v(-34.39, -20.27) * mm, "end": v(-34.38, -20.28) * mm});
            skLineSegment(sketch, "E257.68", {"start": v(-34.84, -19.55) * mm, "end": v(-34.39, -20.27) * mm});
            skLineSegment(sketch, "E257.69", {"start": v(-35.21, -18.62) * mm, "end": v(-34.84, -19.55) * mm});
            skLineSegment(sketch, "E257.70", {"start": v(-35.33, -18.28) * mm, "end": v(-35.21, -18.62) * mm});
            skLineSegment(sketch, "E257.71", {"start": v(-35.44, -17.86) * mm, "end": v(-35.33, -18.28) * mm});
            skLineSegment(sketch, "E257.72", {"start": v(-35.52, -17.55) * mm, "end": v(-35.44, -17.86) * mm});
            skLineSegment(sketch, "E257.73", {"start": v(-35.8, -16.28) * mm, "end": v(-35.52, -17.55) * mm});
            skLineSegment(sketch, "E257.74", {"start": v(-37.24, -9.61) * mm, "end": v(-35.8, -16.28) * mm});
            skLineSegment(sketch, "E257.75", {"start": v(-37.47, -8.57) * mm, "end": v(-37.24, -9.61) * mm});
            skLineSegment(sketch, "E257.76", {"start": v(-37.6, -7.99) * mm, "end": v(-37.47, -8.57) * mm});
            skLineSegment(sketch, "E257.77", {"start": v(-37.67, -7.67) * mm, "end": v(-37.6, -7.99) * mm});
            skLineSegment(sketch, "E257.78", {"start": v(-37.71, -7.43) * mm, "end": v(-37.67, -7.67) * mm});
            skLineSegment(sketch, "E257.79", {"start": v(-37.93, -6.12) * mm, "end": v(-37.71, -7.43) * mm});
            skLineSegment(sketch, "E257.80", {"start": v(-37.94, -6) * mm, "end": v(-37.93, -6.12) * mm});
            skLineSegment(sketch, "E257.81", {"start": v(-37.97, -5.73) * mm, "end": v(-37.94, -6) * mm});
            skLineSegment(sketch, "E257.82", {"start": v(-38.01, -5.3) * mm, "end": v(-37.97, -5.73) * mm});
            skLineSegment(sketch, "E257.83", {"start": v(-38.09, -4.57) * mm, "end": v(-38.01, -5.3) * mm});
            skLineSegment(sketch, "E257.84", {"start": v(-38.11, -3.8) * mm, "end": v(-38.09, -4.57) * mm});
            skLineSegment(sketch, "E257.85", {"start": v(-38.1, -3.03) * mm, "end": v(-38.11, -3.8) * mm});
            skLineSegment(sketch, "E257.86", {"start": v(-38.04, -1.2) * mm, "end": v(-38.1, -3.03) * mm});
            skLineSegment(sketch, "E257.87", {"start": v(-37.99, -0.77) * mm, "end": v(-38.04, -1.2) * mm});
            skLineSegment(sketch, "E257.88", {"start": v(-37.96, -0.48) * mm, "end": v(-37.99, -0.77) * mm});
            skLineSegment(sketch, "E257.89", {"start": v(-30.34, 20.53) * mm, "end": v(-31.42, 19.64) * mm});
            skLineSegment(sketch, "E257.90", {"start": v(-30, 20.79) * mm, "end": v(-30.34, 20.53) * mm});
            skLineSegment(sketch, "E257.91", {"start": v(-29.68, 20.95) * mm, "end": v(-30, 20.79) * mm});
            skLineSegment(sketch, "E257.92", {"start": v(-29.6, 20.99) * mm, "end": v(-29.68, 20.95) * mm});
            skLineSegment(sketch, "E257.93", {"start": v(-29.07, 21.27) * mm, "end": v(-29.6, 20.99) * mm});
            skLineSegment(sketch, "E257.94", {"start": v(-28.98, 21.31) * mm, "end": v(-29.07, 21.27) * mm});
            skLineSegment(sketch, "E257.95", {"start": v(-28.82, 21.4) * mm, "end": v(-28.98, 21.31) * mm});
            skLineSegment(sketch, "E257.96", {"start": v(-28.46, 21.51) * mm, "end": v(-28.82, 21.4) * mm});
            skLineSegment(sketch, "E257.97", {"start": v(-28.42, 21.52) * mm, "end": v(-28.46, 21.51) * mm});
            skLineSegment(sketch, "E257.98", {"start": v(-28.07, 21.64) * mm, "end": v(-28.42, 21.52) * mm});
            skLineSegment(sketch, "E257.99", {"start": v(-27.8, 21.73) * mm, "end": v(-28.07, 21.64) * mm});
            skLineSegment(sketch, "E257.100", {"start": v(-27.3, 21.84) * mm, "end": v(-27.8, 21.73) * mm});
            skLineSegment(sketch, "E257.101", {"start": v(-22.1, 22.01) * mm, "end": v(-24.58, 22) * mm});
            skLineSegment(sketch, "E257.102", {"start": v(-16.38, 22) * mm, "end": v(-22.1, 22.01) * mm});
            skLineSegment(sketch, "E257.103", {"start": v(-15.55, 22) * mm, "end": v(-16.38, 22) * mm});
            skLineSegment(sketch, "E257.104", {"start": v(-13.33, 22.04) * mm, "end": v(-15.55, 22) * mm});
            skLineSegment(sketch, "E257.105", {"start": v(-24.58, 22) * mm, "end": v(-25.85, 22) * mm});
            skLineSegment(sketch, "E257.106", {"start": v(-25.85, 22) * mm, "end": v(-26.72, 21.92) * mm});
            skLineSegment(sketch, "E257.107", {"start": v(-26.72, 21.92) * mm, "end": v(-27.05, 21.9) * mm});
            skLineSegment(sketch, "E257.108", {"start": v(-27.05, 21.9) * mm, "end": v(-27.23, 21.85) * mm});
            skLineSegment(sketch, "E257.109", {"start": v(-27.23, 21.85) * mm, "end": v(-27.28, 21.84) * mm});
            skLineSegment(sketch, "E257.110", {"start": v(-27.28, 21.84) * mm, "end": v(-27.3, 21.84) * mm});
            skLineSegment(sketch, "E257.111", {"start": v(-31.42, 19.64) * mm, "end": v(-31.98, 18.96) * mm});
            skLineSegment(sketch, "E257.112", {"start": v(-31.98, 18.96) * mm, "end": v(-32.1, 18.82) * mm});
            skLineSegment(sketch, "E257.113", {"start": v(-32.1, 18.82) * mm, "end": v(-32.29, 18.6) * mm});
            skLineSegment(sketch, "E257.114", {"start": v(-32.29, 18.6) * mm, "end": v(-32.43, 18.37) * mm});
            skLineSegment(sketch, "E257.115", {"start": v(-32.43, 18.37) * mm, "end": v(-32.58, 18.15) * mm});
            skLineSegment(sketch, "E257.116", {"start": v(-32.58, 18.15) * mm, "end": v(-32.66, 18.01) * mm});
            skLineSegment(sketch, "E257.117", {"start": v(-32.66, 18.01) * mm, "end": v(-32.72, 17.9) * mm});
            skLineSegment(sketch, "E257.118", {"start": v(-32.72, 17.9) * mm, "end": v(-33.02, 17.29) * mm});
            skLineSegment(sketch, "E257.119", {"start": v(-33.02, 17.29) * mm, "end": v(-33.31, 16.68) * mm});
            skLineSegment(sketch, "E257.120", {"start": v(-33.31, 16.68) * mm, "end": v(-33.31, 16.56) * mm});
            skLineSegment(sketch, "E257.121", {"start": v(-33.31, 16.56) * mm, "end": v(-33.33, 16.51) * mm});
            skLineSegment(sketch, "E257.122", {"start": v(-33.33, 16.51) * mm, "end": v(-33.42, 16.25) * mm});
            skLineSegment(sketch, "E257.123", {"start": v(-33.42, 16.25) * mm, "end": v(-33.5, 15.94) * mm});
            skLineSegment(sketch, "E257.124", {"start": v(-33.5, 15.94) * mm, "end": v(-33.81, 14.88) * mm});
            skLineSegment(sketch, "E257.125", {"start": v(-33.81, 14.88) * mm, "end": v(-34.7, 11.83) * mm});
            skLineSegment(sketch, "E257.126", {"start": v(-34.7, 11.83) * mm, "end": v(-35.87, 7.75) * mm});
            skLineSegment(sketch, "E257.127", {"start": v(-35.87, 7.75) * mm, "end": v(-36.27, 6.34) * mm});
            skLineSegment(sketch, "E257.128", {"start": v(-36.27, 6.34) * mm, "end": v(-36.89, 4.21) * mm});
            skLineSegment(sketch, "E257.129", {"start": v(-36.89, 4.21) * mm, "end": v(-37.41, 2.38) * mm});
            skLineSegment(sketch, "E257.130", {"start": v(-37.41, 2.38) * mm, "end": v(-37.44, 2.28) * mm});
            skLineSegment(sketch, "E257.131", {"start": v(-37.44, 2.28) * mm, "end": v(-37.54, 1.85) * mm});
            skLineSegment(sketch, "E257.132", {"start": v(-37.54, 1.85) * mm, "end": v(-37.9, 0) * mm});
            skLineSegment(sketch, "E257.133", {"start": v(-37.9, 0) * mm, "end": v(-37.91, -0.09) * mm});
            skLineSegment(sketch, "E257.134", {"start": v(-37.91, -0.09) * mm, "end": v(-37.96, -0.48) * mm});
            skLineSegment(sketch, "E257.135", {"start": v(0.52, -24) * mm, "end": v(2.71, -24) * mm});
            skLineSegment(sketch, "E257.136", {"start": v(2.71, -24) * mm, "end": v(8.2, -24) * mm});
            skLineSegment(sketch, "E257.137", {"start": v(8.2, -24) * mm, "end": v(16.38, -24) * mm});
            skLineSegment(sketch, "E257.138", {"start": v(16.38, -24) * mm, "end": v(23.58, -24) * mm});
            skLineSegment(sketch, "E257.139", {"start": v(23.58, -24) * mm, "end": v(24.59, -23.99) * mm});
            skLineSegment(sketch, "E257.140", {"start": v(24.59, -23.99) * mm, "end": v(26.87, -23.97) * mm});
            skLineSegment(sketch, "E257.141", {"start": v(26.87, -23.97) * mm, "end": v(28.23, -23.96) * mm});
            skLineSegment(sketch, "E257.142", {"start": v(28.23, -23.96) * mm, "end": v(28.38, -23.96) * mm});
            skLineSegment(sketch, "E257.143", {"start": v(28.38, -23.96) * mm, "end": v(28.68, -23.92) * mm});
            skLineSegment(sketch, "E257.144", {"start": v(28.68, -23.92) * mm, "end": v(29.58, -23.76) * mm});
            skLineSegment(sketch, "E257.145", {"start": v(29.58, -23.76) * mm, "end": v(29.7, -23.72) * mm});
            skLineSegment(sketch, "E257.146", {"start": v(29.7, -23.72) * mm, "end": v(30.35, -23.51) * mm});
            skLineSegment(sketch, "E257.147", {"start": v(30.35, -23.51) * mm, "end": v(30.67, -23.43) * mm});
            skLineSegment(sketch, "E257.148", {"start": v(30.67, -23.43) * mm, "end": v(30.83, -23.33) * mm});
            skLineSegment(sketch, "E257.149", {"start": v(30.83, -23.33) * mm, "end": v(30.93, -23.29) * mm});
            skLineSegment(sketch, "E257.150", {"start": v(30.93, -23.29) * mm, "end": v(31, -23.25) * mm});
            skLineSegment(sketch, "E257.151", {"start": v(31, -23.25) * mm, "end": v(31.22, -23.15) * mm});
            skLineSegment(sketch, "E257.152", {"start": v(31.22, -23.15) * mm, "end": v(31.54, -23) * mm});
            skLineSegment(sketch, "E257.153", {"start": v(31.54, -23) * mm, "end": v(31.7, -22.9) * mm});
            skLineSegment(sketch, "E257.154", {"start": v(31.7, -22.9) * mm, "end": v(32, -22.69) * mm});
            skLineSegment(sketch, "E257.155", {"start": v(32, -22.69) * mm, "end": v(32.37, -22.44) * mm});
            skLineSegment(sketch, "E257.156", {"start": v(32.37, -22.44) * mm, "end": v(32.66, -22.25) * mm});
            skLineSegment(sketch, "E257.157", {"start": v(32.66, -22.25) * mm, "end": v(33.16, -21.8) * mm});
            skLineSegment(sketch, "E257.158", {"start": v(33.16, -21.8) * mm, "end": v(33.33, -21.65) * mm});
            skLineSegment(sketch, "E257.159", {"start": v(33.33, -21.65) * mm, "end": v(33.44, -21.52) * mm});
            skLineSegment(sketch, "E257.160", {"start": v(33.44, -21.52) * mm, "end": v(33.49, -21.47) * mm});
            skLineSegment(sketch, "E257.161", {"start": v(33.49, -21.47) * mm, "end": v(33.87, -21) * mm});
            skLineSegment(sketch, "E257.162", {"start": v(33.87, -21) * mm, "end": v(33.97, -20.9) * mm});
            skLineSegment(sketch, "E257.163", {"start": v(33.97, -20.9) * mm, "end": v(34.2, -20.62) * mm});
            skLineSegment(sketch, "E257.164", {"start": v(34.2, -20.62) * mm, "end": v(34.44, -20.23) * mm});
            skLineSegment(sketch, "E257.165", {"start": v(34.44, -20.23) * mm, "end": v(34.47, -20.18) * mm});
            skLineSegment(sketch, "E257.166", {"start": v(34.47, -20.18) * mm, "end": v(34.47, -20.17) * mm});
            skLineSegment(sketch, "E257.167", {"start": v(34.47, -20.17) * mm, "end": v(34.7, -19.8) * mm});
            skLineSegment(sketch, "E257.168", {"start": v(34.7, -19.8) * mm, "end": v(34.84, -19.5) * mm});
            skLineSegment(sketch, "E257.169", {"start": v(34.84, -19.5) * mm, "end": v(34.87, -19.44) * mm});
            skLineSegment(sketch, "E257.170", {"start": v(34.87, -19.44) * mm, "end": v(35.09, -18.97) * mm});
            skLineSegment(sketch, "E257.171", {"start": v(35.09, -18.97) * mm, "end": v(35.14, -18.8) * mm});
            skLineSegment(sketch, "E257.172", {"start": v(35.14, -18.8) * mm, "end": v(35.19, -18.67) * mm});
            skLineSegment(sketch, "E257.173", {"start": v(35.19, -18.67) * mm, "end": v(35.24, -18.49) * mm});
            skLineSegment(sketch, "E257.174", {"start": v(35.24, -18.49) * mm, "end": v(35.28, -18.45) * mm});
            skLineSegment(sketch, "E257.175", {"start": v(35.28, -18.45) * mm, "end": v(35.5, -17.59) * mm});
            skLineSegment(sketch, "E257.176", {"start": v(35.5, -17.59) * mm, "end": v(36.04, -15.09) * mm});
            skLineSegment(sketch, "E257.177", {"start": v(36.04, -15.09) * mm, "end": v(37.24, -9.61) * mm});
            skLineSegment(sketch, "E257.178", {"start": v(37.24, -9.61) * mm, "end": v(37.46, -8.58) * mm});
            skLineSegment(sketch, "E257.179", {"start": v(37.46, -8.58) * mm, "end": v(37.72, -7.3) * mm});
            skLineSegment(sketch, "E257.180", {"start": v(37.72, -7.3) * mm, "end": v(37.74, -7.18) * mm});
            skLineSegment(sketch, "E257.181", {"start": v(37.74, -7.18) * mm, "end": v(37.84, -6.7) * mm});
            skLineSegment(sketch, "E257.182", {"start": v(37.84, -6.7) * mm, "end": v(37.9, -6.33) * mm});
            skLineSegment(sketch, "E257.183", {"start": v(37.9, -6.33) * mm, "end": v(37.97, -5.68) * mm});
            skLineSegment(sketch, "E257.184", {"start": v(37.97, -5.68) * mm, "end": v(38.02, -5.37) * mm});
            skLineSegment(sketch, "E257.185", {"start": v(38.02, -5.37) * mm, "end": v(38.03, -5.24) * mm});
            skLineSegment(sketch, "E257.186", {"start": v(38.03, -5.24) * mm, "end": v(38.04, -5.06) * mm});
            skLineSegment(sketch, "E257.187", {"start": v(38.04, -5.06) * mm, "end": v(38.11, -3.87) * mm});
            skLineSegment(sketch, "E257.188", {"start": v(38.11, -3.87) * mm, "end": v(38.1, -3.48) * mm});
            skLineSegment(sketch, "E257.189", {"start": v(38.1, -3.48) * mm, "end": v(38.07, -1.76) * mm});
            skLineSegment(sketch, "E257.190", {"start": v(38.07, -1.76) * mm, "end": v(38.07, -1.57) * mm});
            skLineSegment(sketch, "E257.191", {"start": v(38.07, -1.57) * mm, "end": v(37.98, -0.78) * mm});
            skLineSegment(sketch, "E257.192", {"start": v(37.98, -0.78) * mm, "end": v(37.96, -0.52) * mm});
            skLineSegment(sketch, "E257.193", {"start": v(37.96, -0.52) * mm, "end": v(37.96, -0.52) * mm});
            skLineSegment(sketch, "E257.194", {"start": v(37.96, -0.52) * mm, "end": v(37.91, -0.1) * mm});
            skLineSegment(sketch, "E257.195", {"start": v(37.91, -0.1) * mm, "end": v(37.81, 0.37) * mm});
            skLineSegment(sketch, "E257.196", {"start": v(37.81, 0.37) * mm, "end": v(37.58, 1.66) * mm});
            skLineSegment(sketch, "E257.197", {"start": v(37.58, 1.66) * mm, "end": v(37.32, 2.7) * mm});
            skLineSegment(sketch, "E257.198", {"start": v(37.32, 2.7) * mm, "end": v(36.84, 4.4) * mm});
            skLineSegment(sketch, "E257.199", {"start": v(36.84, 4.4) * mm, "end": v(36.52, 5.5) * mm});
            skLineSegment(sketch, "E257.200", {"start": v(36.52, 5.5) * mm, "end": v(36.36, 6.06) * mm});
            skLineSegment(sketch, "E257.201", {"start": v(36.36, 6.06) * mm, "end": v(35.87, 7.75) * mm});
            skLineSegment(sketch, "E257.202", {"start": v(35.87, 7.75) * mm, "end": v(34.69, 11.84) * mm});
            skLineSegment(sketch, "E257.203", {"start": v(34.69, 11.84) * mm, "end": v(33.5, 15.94) * mm});
            skLineSegment(sketch, "E257.204", {"start": v(33.5, 15.94) * mm, "end": v(33.4, 16.3) * mm});
            skLineSegment(sketch, "E257.205", {"start": v(33.4, 16.3) * mm, "end": v(33.04, 17.23) * mm});
            skLineSegment(sketch, "E257.206", {"start": v(33.04, 17.23) * mm, "end": v(33, 17.34) * mm});
            skLineSegment(sketch, "E257.207", {"start": v(33, 17.34) * mm, "end": v(32.94, 17.5) * mm});
            skLineSegment(sketch, "E257.208", {"start": v(32.94, 17.5) * mm, "end": v(32.5, 18.25) * mm});
            skLineSegment(sketch, "E257.209", {"start": v(32.5, 18.25) * mm, "end": v(32.33, 18.54) * mm});
            skLineSegment(sketch, "E257.210", {"start": v(32.33, 18.54) * mm, "end": v(32.19, 18.7) * mm});
            skLineSegment(sketch, "E257.211", {"start": v(32.19, 18.7) * mm, "end": v(31.7, 19.35) * mm});
            skLineSegment(sketch, "E257.212", {"start": v(31.7, 19.35) * mm, "end": v(31.2, 19.84) * mm});
            skLineSegment(sketch, "E257.213", {"start": v(31.2, 19.84) * mm, "end": v(31.12, 19.93) * mm});
            skLineSegment(sketch, "E257.214", {"start": v(31.12, 19.93) * mm, "end": v(30.7, 20.25) * mm});
            skLineSegment(sketch, "E257.215", {"start": v(30.7, 20.25) * mm, "end": v(30.68, 20.27) * mm});
            skLineSegment(sketch, "E257.216", {"start": v(30.68, 20.27) * mm, "end": v(30.02, 20.77) * mm});
            skLineSegment(sketch, "E257.217", {"start": v(30.02, 20.77) * mm, "end": v(29.84, 20.87) * mm});
            skLineSegment(sketch, "E257.218", {"start": v(29.84, 20.87) * mm, "end": v(29.61, 20.99) * mm});
            skLineSegment(sketch, "E257.219", {"start": v(29.61, 20.99) * mm, "end": v(29.56, 21) * mm});
            skLineSegment(sketch, "E257.220", {"start": v(29.56, 21) * mm, "end": v(29.06, 21.27) * mm});
            skLineSegment(sketch, "E257.221", {"start": v(29.06, 21.27) * mm, "end": v(28.8, 21.4) * mm});
            skLineSegment(sketch, "E257.222", {"start": v(28.8, 21.4) * mm, "end": v(28.42, 21.54) * mm});
            skLineSegment(sketch, "E257.223", {"start": v(28.42, 21.54) * mm, "end": v(28.26, 21.57) * mm});
            skLineSegment(sketch, "E257.224", {"start": v(28.26, 21.57) * mm, "end": v(28.18, 21.6) * mm});
            skLineSegment(sketch, "E257.225", {"start": v(28.18, 21.6) * mm, "end": v(27.93, 21.68) * mm});
            skLineSegment(sketch, "E257.226", {"start": v(27.93, 21.68) * mm, "end": v(27.78, 21.73) * mm});
            skLineSegment(sketch, "E257.227", {"start": v(27.78, 21.73) * mm, "end": v(27.43, 21.83) * mm});
            skLineSegment(sketch, "E257.228", {"start": v(27.43, 21.83) * mm, "end": v(27.03, 21.86) * mm});
            skLineSegment(sketch, "E257.229", {"start": v(27.03, 21.86) * mm, "end": v(26.61, 21.93) * mm});
            skLineSegment(sketch, "E257.230", {"start": v(26.61, 21.93) * mm, "end": v(26.26, 21.99) * mm});
            skLineSegment(sketch, "E257.231", {"start": v(26.26, 21.99) * mm, "end": v(25.87, 22) * mm});
            skLineSegment(sketch, "E257.232", {"start": v(25.87, 22) * mm, "end": v(25.76, 22) * mm});
            skLineSegment(sketch, "E257.233", {"start": v(25.76, 22) * mm, "end": v(17.39, 22) * mm});
            skLineSegment(sketch, "E257.234", {"start": v(17.39, 22) * mm, "end": v(16.4, 22.02) * mm});
            skLineSegment(sketch, "E257.235", {"start": v(16.4, 22.02) * mm, "end": v(13.98, 22.04) * mm});
            skLineSegment(sketch, "E257.236", {"start": v(13.98, 22.04) * mm, "end": v(13.36, 22.04) * mm});
            skSolve(sketch);
        }
        {
            var Q0;
            Q0 = qSketchRegion(id + "F3", true);
            extrude(context, id + "F4", {"entities" : qUnion([Q0]), "operationType" : NewBodyOperationType.ADD, "depth" : 15 * mm});
        }
        {
            var Q0;
            Q0 = qSketchRegion(id + "F2", true);
            extrude(context, id + "F5", {"entities" : qUnion([Q0]), "operationType" : NewBodyOperationType.REMOVE, "depth" : 25 * mm, "hasSecondDirection" : true, "secondDirectionOppositeDirection" : true, "secondDirectionDepth" : 25 * mm});
        }
    });
